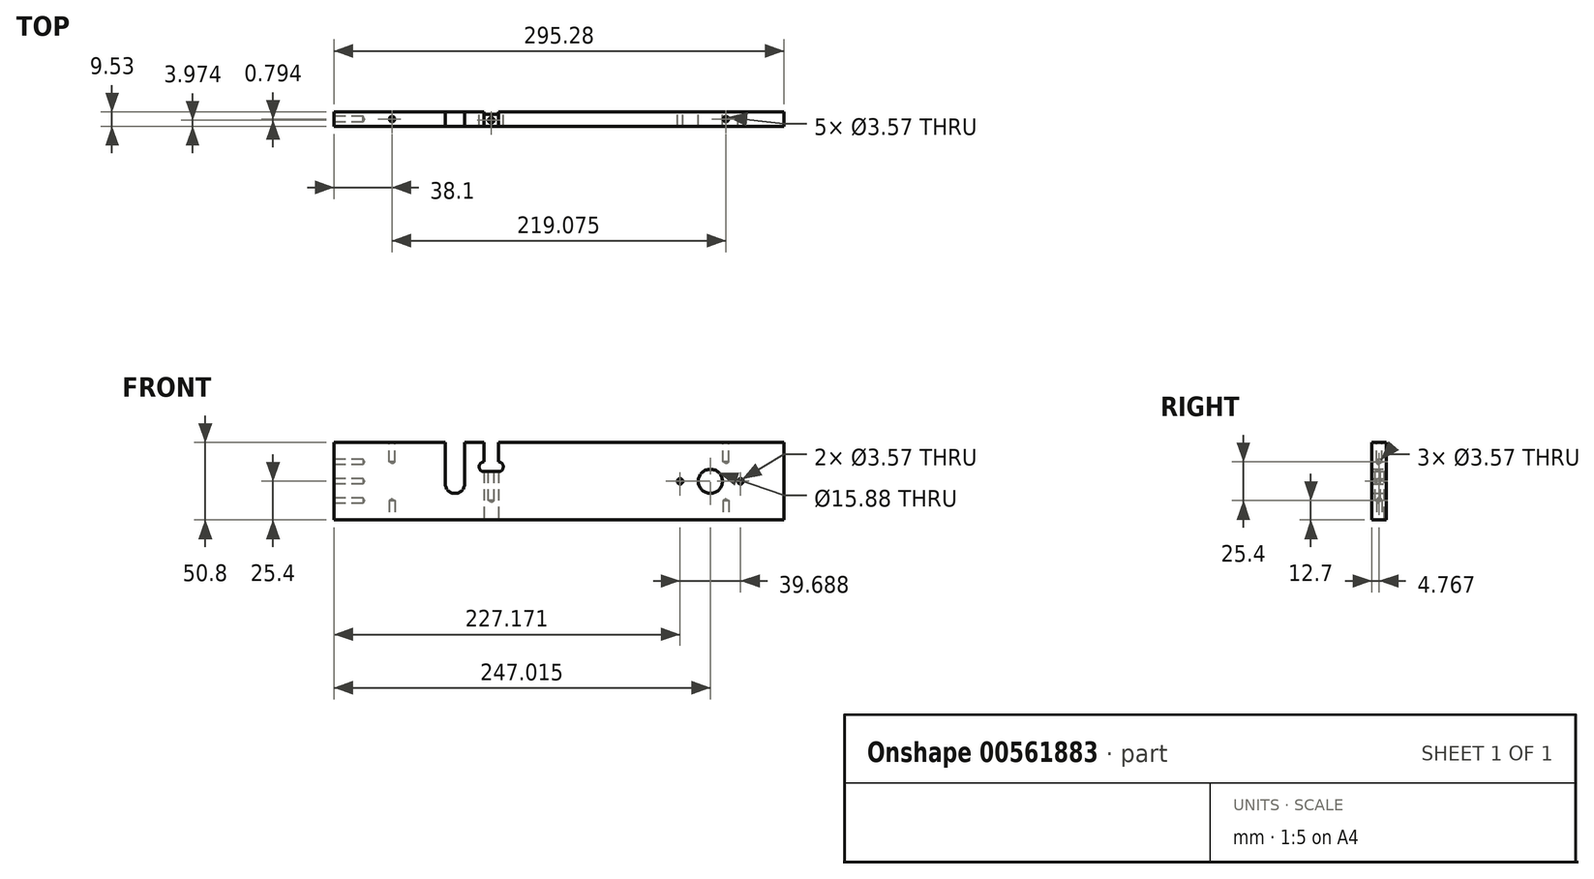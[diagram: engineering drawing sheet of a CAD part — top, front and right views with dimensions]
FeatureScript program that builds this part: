
annotation { "Feature Type Name" : "Feature", "Feature Type Description" : "" }
export const myFeature = defineFeature(function(context is Context, id is Id, definition is map)
    precondition{}
    {
        {
            var Q0;
            Q0=qCreatedBy(makeId("Front.planeOp"),FACE);
            var sketch = newSketch(context, id + "F0", { "sketchPlane" : qUnion([Q0])});
            skLineSegment(sketch, "E0", {"start": v(0, 0) * mm, "end": v(295.28, 0) * mm});
            skLineSegment(sketch, "E1", {"start": v(295.28, 0) * mm, "end": v(295.28, 50.8) * mm});
            skLineSegment(sketch, "E2", {"start": v(0, 50.8) * mm, "end": v(0, 0) * mm});
            skLineSegment(sketch, "E3", {"start": v(0, 50.8) * mm, "end": v(98.43, 50.8) * mm});
            skLineSegment(sketch, "E4", {"start": v(98.43, 50.8) * mm, "end": v(98.43, 31.75) * mm});
            skLineSegment(sketch, "E5", {"start": v(107.96, 50.8) * mm, "end": v(107.96, 31.75) * mm});
            skLineSegment(sketch, "E6", {"start": v(98.43, 31.75) * mm, "end": v(107.96, 31.75) * mm});
            skLineSegment(sketch, "E7", {"start": v(107.96, 50.8) * mm, "end": v(295.28, 50.8) * mm});
            skCircle(sketch, "E8", {"center": v(79.38, 23.81) * mm, "radius": 6.35 * mm});
            skLineSegment(sketch, "E9", {"start": v(73.02, 50.8) * mm, "end": v(73.02, 23.81) * mm});
            skLineSegment(sketch, "E10", {"start": v(85.72, 50.8) * mm, "end": v(85.72, 23.81) * mm});
            skLineSegment(sketch, "E11", {"start": v(79.38, 50.8) * mm, "end": v(79.38, 0) * mm, "construction": true});
            skArc(sketch, "E12", {"start": v(98.43, 38.1) * mm, "mid": v(95.25, 34.93) * mm, "end": v(98.43, 31.75) * mm});
            skArc(sketch, "E13", {"start": v(107.96, 31.75) * mm, "mid": v(111.14, 34.93) * mm, "end": v(107.96, 38.1) * mm});
            skCircle(sketch, "E14", {"center": v(79.38, 23.81) * mm, "radius": 38.1 * mm, "construction": true});
            skCircle(sketch, "E15", {"center": v(247.02, 25.4) * mm, "radius": 38.99 * mm, "construction": true});
            skLineSegment(sketch, "E16", {"start": v(247.02, 50.8) * mm, "end": v(247.02, 0) * mm, "construction": true});
            skCircle(sketch, "E17", {"center": v(247.02, 25.4) * mm, "radius": 7.94 * mm});
            skLineSegment(sketch, "E18", {"start": v(227.17, 25.4) * mm, "end": v(247.02, 25.4) * mm, "construction": true});
            skLineSegment(sketch, "E19", {"start": v(266.86, 25.4) * mm, "end": v(247.02, 25.4) * mm, "construction": true});
            skCircle(sketch, "E20", {"center": v(227.17, 25.4) * mm, "radius": 1.79 * mm});
            skCircle(sketch, "E21", {"center": v(266.86, 25.4) * mm, "radius": 1.79 * mm});
            skSolve(sketch);
        }
        {
            var Q0;
            Q0=makeQuery(id+"F0.imprint","IMPRINT",FACE,{"disambiguationData":[TD([[makeQuery(id+"F0.imprint","IMPRINT",EDGE,{"derivedFrom":sQuery(id+"F0.wireOp",EDGE,"E0")}),1.0]])]});
            extrude(context, id + "F1", {"entities" : qUnion([Q0]), "depth" : 9.52 * mm, "offsetDistance" : 25.4 * mm});
        }
        {
            var Q0;
            Q0=makeQuery(id+"F1.opExtrude","CAP_FACE",FACE,{"disambiguationData":[OSD([sQuery(id+"F0.wireOp",EDGE,"E0"),sQuery(id+"F0.wireOp",EDGE,"E1"),sQuery(id+"F0.wireOp",EDGE,"E2"),sQuery(id+"F0.wireOp",EDGE,"E3"),sQuery(id+"F0.wireOp",EDGE,"E4"),sQuery(id+"F0.wireOp",EDGE,"E5"),sQuery(id+"F0.wireOp",EDGE,"E6"),sQuery(id+"F0.wireOp",EDGE,"E7")])],"isStart":true});
            var sketch = newSketch(context, id + "F2", { "sketchPlane" : qUnion([Q0])});
            skLineSegment(sketch, "E22.bottom", {"start": v(-107.96, 31.75) * mm, "end": v(-98.43, 31.75) * mm});
            skLineSegment(sketch, "E22.top", {"start": v(-107.96, 0) * mm, "end": v(-98.43, 0) * mm});
            skLineSegment(sketch, "E22.left", {"start": v(-107.96, 31.75) * mm, "end": v(-107.96, 0) * mm});
            skLineSegment(sketch, "E22.right", {"start": v(-98.43, 31.75) * mm, "end": v(-98.43, 0) * mm});
            skSolve(sketch);
        }
        {
            var Q0;
            Q0 = qSketchRegion(id + "F2", true);
            extrude(context, id + "F3", {"entities" : qUnion([Q0]), "operationType" : NewBodyOperationType.REMOVE, "oppositeDirection" : true, "depth" : 1.59 * mm, "offsetDistance" : 25.4 * mm});
        }
        {
            var Q0;
            Q0=makeQuery(id+"F1.opExtrude","SWEPT_FACE",FACE,{"disambiguationData":[OSD([sQuery(id+"F0.wireOp",EDGE,"E2")])]});
            var sketch = newSketch(context, id + "F4", { "sketchPlane" : qUnion([Q0])});
            skLineSegment(sketch, "E23", {"start": v(4.76, 50.8) * mm, "end": v(4.76, 0) * mm, "construction": true});
            skLineSegment(sketch, "E24", {"start": v(0, 25.4) * mm, "end": v(9.53, 25.4) * mm, "construction": true});
            skPoint(sketch, "E25", {"position": v(4.76, 25.4) * mm});
            skPoint(sketch, "E26", {"position": v(4.76, 38.1) * mm});
            skPoint(sketch, "E27", {"position": v(4.76, 12.7) * mm});
            skSolve(sketch);
        }
        {
            var Q0;
            Q0=sQuery(id+"F4.wireOp",VERTEX,"E26");
            var Q1;
            Q1=sQuery(id+"F4.wireOp",VERTEX,"E25");
            var Q2;
            Q2=sQuery(id+"F4.wireOp",VERTEX,"E27");
            var Q3;
            Q3=makeQuery(id+"F1.opExtrude","SWEPT_BODY",BODY,{"disambiguationData":[OSD([sQuery(id+"F0.wireOp",EDGE,"E0"),sQuery(id+"F0.wireOp",EDGE,"E1"),sQuery(id+"F0.wireOp",EDGE,"E2"),sQuery(id+"F0.wireOp",EDGE,"E3"),sQuery(id+"F0.wireOp",EDGE,"E4"),sQuery(id+"F0.wireOp",EDGE,"E5"),sQuery(id+"F0.wireOp",EDGE,"E6"),sQuery(id+"F0.wireOp",EDGE,"E7"),sQuery(id+"F0.wireOp",EDGE,"E8"),sQuery(id+"F0.wireOp",EDGE,"E9"),sQuery(id+"F0.wireOp",EDGE,"E10"),sQuery(id+"F0.wireOp",EDGE,"E12"),sQuery(id+"F0.wireOp",EDGE,"E13"),sQuery(id+"F0.wireOp",EDGE,"E17")])]});
            hole(context, id + "F5", {"style" : HoleStyle.SIMPLE, "endStyle" : HoleEndStyle.BLIND, "holeDiameter" : 3.57 * mm, "majorDiameter" : 6.35 * mm, "holeDepth" : 19.05 * mm, "isTappedThrough" : true, "tappedDepth" : 12.7 * mm, "tapClearance" : 3, "startFromSketch" : true, "locations" : qUnion([Q0, Q1, Q2]), "scope" : qUnion([Q3])});
        }
        {
            var Q0;
            Q0=makeQuery(id+"F1.opExtrude","SWEPT_FACE",FACE,{"disambiguationData":[OSD([sQuery(id+"F0.wireOp",EDGE,"E6")])]});
            var sketch = newSketch(context, id + "F6", { "sketchPlane" : qUnion([Q0])});
            skLineSegment(sketch, "E28", {"start": v(98.43, -1.59) * mm, "end": v(107.96, -9.53) * mm, "construction": true});
            skLineSegment(sketch, "E29", {"start": v(107.96, -1.59) * mm, "end": v(98.43, -9.52) * mm, "construction": true});
            skPoint(sketch, "E30", {"position": v(103.2, -5.56) * mm});
            skSolve(sketch);
        }
        {
            var Q0;
            Q0=sQuery(id+"F6.wireOp",VERTEX,"fac4ed8d-bee8-4eeb-a691-8f1f0a51aa8e.positionSnap0");
            var Q1;
            Q1=sQuery(id+"F6.wireOp",VERTEX,"E30");
            var Q2;
            Q2=makeQuery(id+"F1.opExtrude","SWEPT_BODY",BODY,{"disambiguationData":[OSD([sQuery(id+"F0.wireOp",EDGE,"E0"),sQuery(id+"F0.wireOp",EDGE,"E1"),sQuery(id+"F0.wireOp",EDGE,"E2"),sQuery(id+"F0.wireOp",EDGE,"E3"),sQuery(id+"F0.wireOp",EDGE,"E4"),sQuery(id+"F0.wireOp",EDGE,"E5"),sQuery(id+"F0.wireOp",EDGE,"E6"),sQuery(id+"F0.wireOp",EDGE,"E7"),sQuery(id+"F0.wireOp",EDGE,"E8"),sQuery(id+"F0.wireOp",EDGE,"E9"),sQuery(id+"F0.wireOp",EDGE,"E10"),sQuery(id+"F0.wireOp",EDGE,"E12"),sQuery(id+"F0.wireOp",EDGE,"E13"),sQuery(id+"F0.wireOp",EDGE,"E17")])]});
            hole(context, id + "F7", {"style" : HoleStyle.SIMPLE, "endStyle" : HoleEndStyle.BLIND, "holeDiameter" : 3.57 * mm, "majorDiameter" : 6.35 * mm, "holeDepth" : 19.05 * mm, "isTappedThrough" : true, "tappedDepth" : 12.7 * mm, "tapClearance" : 3, "startFromSketch" : true, "locations" : qUnion([Q0, Q1]), "scope" : qUnion([Q2])});
        }
        {
            var Q0;
            Q0=makeQuery(id+"F1.opExtrude","SWEPT_FACE",FACE,{"disambiguationData":[OSD([sQuery(id+"F0.wireOp",EDGE,"E7")])]});
            var sketch = newSketch(context, id + "F8", { "sketchPlane" : qUnion([Q0])});
            skLineSegment(sketch, "E31", {"start": v(295.28, -4.76) * mm, "end": v(257.18, -4.76) * mm});
            skPoint(sketch, "E32", {"position": v(257.18, -4.76) * mm});
            skSolve(sketch);
        }
        {
            var Q0;
            {var subQ0=sQuery(id+"F0.wireOp",EDGE,"E3");Q0=makeQuery(id+"F1.opExtrude","SWEPT_FACE",FACE,{"disambiguationData":[OSD([subQ0]),TDD([makeQuery(id+"F0.imprint","IMPRINT",EDGE,{"disambiguationData":[TD([[makeQuery(id+"F0.imprint","INTERSECT",VERTEX,{"derivedFrom":[sQuery(id+"F0.wireOp",EDGE,"E2"),subQ0]}),-1.0]])],"derivedFrom":subQ0})])]});}
            var sketch = newSketch(context, id + "F9", { "sketchPlane" : qUnion([Q0])});
            skLineSegment(sketch, "E33", {"start": v(0, -4.76) * mm, "end": v(38.1, -4.76) * mm});
            skPoint(sketch, "E34", {"position": v(38.1, -4.76) * mm});
            skSolve(sketch);
        }
        {
            var Q0;
            Q0=makeQuery(id+"F1.opExtrude","SWEPT_FACE",FACE,{"disambiguationData":[OSD([sQuery(id+"F0.wireOp",EDGE,"E0")])]});
            var sketch = newSketch(context, id + "F10", { "sketchPlane" : qUnion([Q0])});
            skLineSegment(sketch, "E35", {"start": v(0, 4.76) * mm, "end": v(38.1, 4.76) * mm});
            skLineSegment(sketch, "E36", {"start": v(295.28, 4.76) * mm, "end": v(257.18, 4.76) * mm});
            skPoint(sketch, "E37", {"position": v(257.18, 4.76) * mm});
            skPoint(sketch, "E38", {"position": v(38.1, 4.76) * mm});
            skSolve(sketch);
        }
        {
            var Q0;
            Q0=sQuery(id+"F8.wireOp",VERTEX,"E32");
            var Q1;
            Q1=sQuery(id+"F9.wireOp",VERTEX,"E34");
            var Q2;
            Q2=sQuery(id+"F10.wireOp",VERTEX,"E38");
            var Q3;
            Q3=sQuery(id+"F10.wireOp",VERTEX,"E37");
            var Q4;
            Q4=makeQuery(id+"F1.opExtrude","SWEPT_BODY",BODY,{"disambiguationData":[OSD([sQuery(id+"F0.wireOp",EDGE,"E0"),sQuery(id+"F0.wireOp",EDGE,"E1"),sQuery(id+"F0.wireOp",EDGE,"E2"),sQuery(id+"F0.wireOp",EDGE,"E3"),sQuery(id+"F0.wireOp",EDGE,"E4"),sQuery(id+"F0.wireOp",EDGE,"E5"),sQuery(id+"F0.wireOp",EDGE,"E6"),sQuery(id+"F0.wireOp",EDGE,"E7"),sQuery(id+"F0.wireOp",EDGE,"E8"),sQuery(id+"F0.wireOp",EDGE,"E9"),sQuery(id+"F0.wireOp",EDGE,"E10"),sQuery(id+"F0.wireOp",EDGE,"E12"),sQuery(id+"F0.wireOp",EDGE,"E13"),sQuery(id+"F0.wireOp",EDGE,"E17")])]});
            hole(context, id + "F11", {"style" : HoleStyle.SIMPLE, "endStyle" : HoleEndStyle.BLIND, "holeDiameter" : 3.57 * mm, "majorDiameter" : 6.35 * mm, "holeDepth" : 12.7 * mm, "isTappedThrough" : true, "tappedDepth" : 12.7 * mm, "tapClearance" : 3, "startFromSketch" : true, "locations" : qUnion([Q0, Q1, Q2, Q3]), "scope" : qUnion([Q4])});
        }
    });
